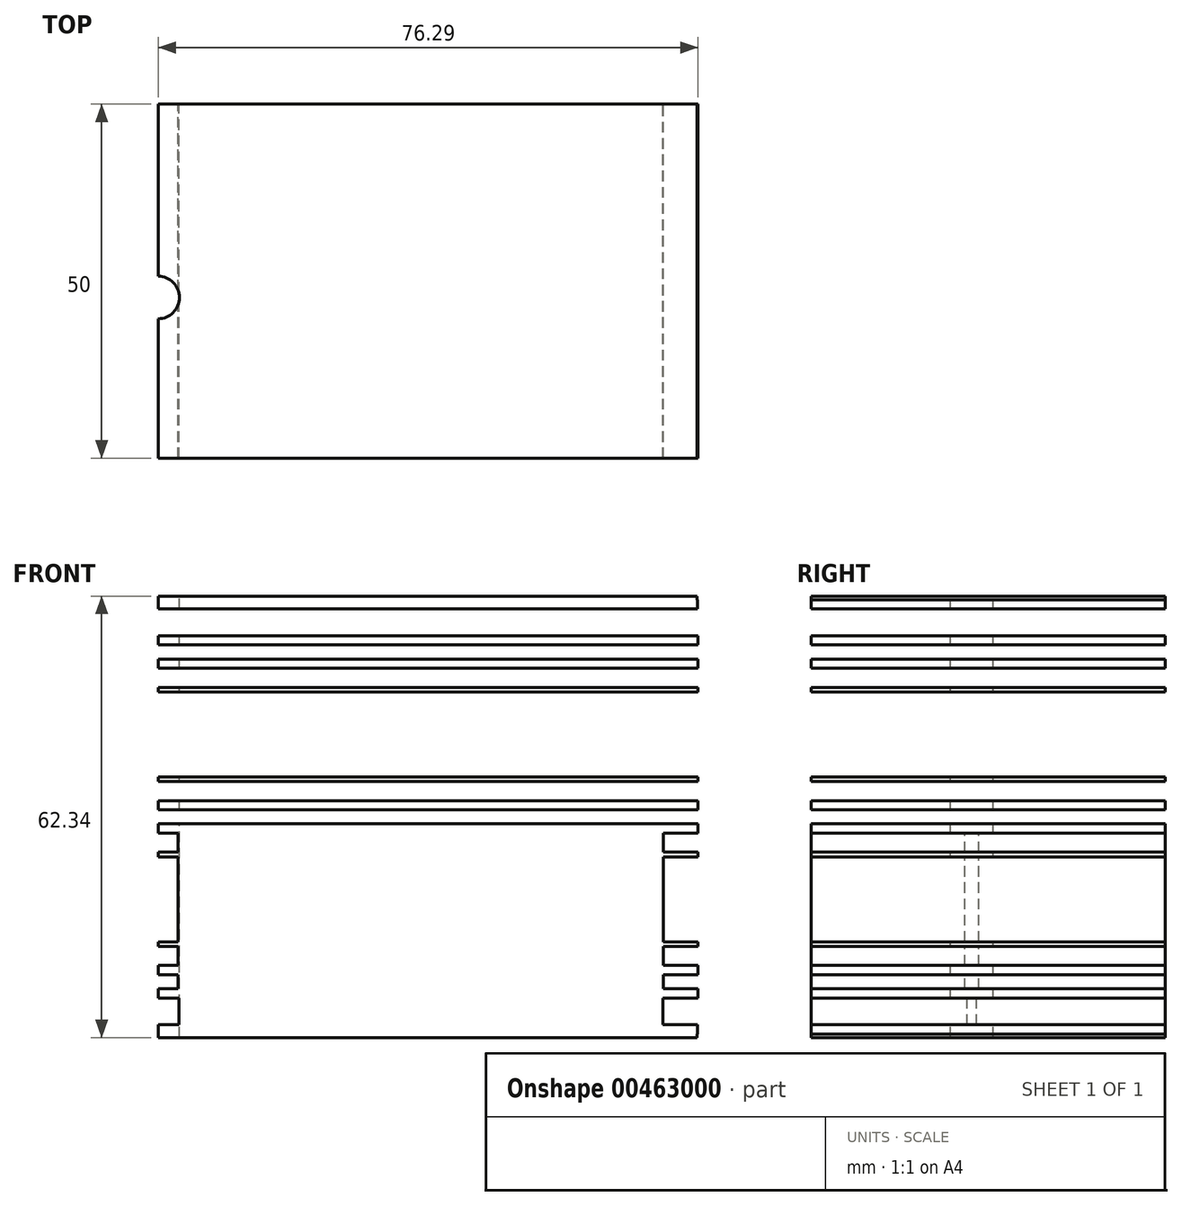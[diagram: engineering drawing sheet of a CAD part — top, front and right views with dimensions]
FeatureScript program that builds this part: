
annotation { "Feature Type Name" : "Feature", "Feature Type Description" : "" }
export const myFeature = defineFeature(function(context is Context, id is Id, definition is map)
    precondition{}
    {
        {
            var Q0;
            Q0=qCreatedBy(makeId("Front.planeOp"),FACE);
            var sketch = newSketch(context, id + "F0", { "sketchPlane" : qUnion([Q0])});
            skLineSegment(sketch, "E0.bottom", {"start": v(0, 0) * mm, "end": v(76.17, 0) * mm});
            skLineSegment(sketch, "E0.top", {"start": v(0, 0.5) * mm, "end": v(76.17, 0.5) * mm});
            skLineSegment(sketch, "E0.left", {"start": v(0, 0) * mm, "end": v(0, 0.5) * mm});
            skLineSegment(sketch, "E0.right", {"start": v(76.17, 0) * mm, "end": v(76.17, 0.5) * mm});
            skLineSegment(sketch, "E1.bottom", {"start": v(0, 0) * mm, "end": v(76.2, 0) * mm});
            skLineSegment(sketch, "E1.top", {"start": v(0, -1.3) * mm, "end": v(76.2, -1.3) * mm});
            skLineSegment(sketch, "E1.left", {"start": v(0, 0) * mm, "end": v(0, -1.3) * mm});
            skLineSegment(sketch, "E1.right", {"start": v(76.2, 0) * mm, "end": v(76.2, -1.3) * mm});
            skLineSegment(sketch, "E2.bottom", {"start": v(2.92, -1.3) * mm, "end": v(71.33, -1.3) * mm});
            skLineSegment(sketch, "E2.top", {"start": v(2.92, -5.07) * mm, "end": v(71.33, -5.07) * mm});
            skLineSegment(sketch, "E2.left", {"start": v(2.92, -1.3) * mm, "end": v(2.92, -5.07) * mm});
            skLineSegment(sketch, "E2.right", {"start": v(71.33, -1.3) * mm, "end": v(71.33, -5.07) * mm});
            skLineSegment(sketch, "E3.bottom", {"start": v(0, -5.07) * mm, "end": v(76.3, -5.07) * mm});
            skLineSegment(sketch, "E3.top", {"start": v(0, -6.37) * mm, "end": v(76.3, -6.37) * mm});
            skLineSegment(sketch, "E3.left", {"start": v(0, -5.07) * mm, "end": v(0, -6.37) * mm});
            skLineSegment(sketch, "E3.right", {"start": v(76.3, -5.07) * mm, "end": v(76.3, -6.37) * mm});
            skLineSegment(sketch, "E4.bottom", {"start": v(2.83, -6.37) * mm, "end": v(71.36, -6.37) * mm});
            skLineSegment(sketch, "E4.top", {"start": v(2.83, -8.37) * mm, "end": v(71.36, -8.37) * mm});
            skLineSegment(sketch, "E4.left", {"start": v(2.83, -6.37) * mm, "end": v(2.83, -8.37) * mm});
            skLineSegment(sketch, "E4.right", {"start": v(71.36, -6.37) * mm, "end": v(71.36, -8.37) * mm});
            skLineSegment(sketch, "E5.bottom", {"start": v(0, -8.37) * mm, "end": v(76.3, -8.37) * mm});
            skLineSegment(sketch, "E5.top", {"start": v(0, -9.67) * mm, "end": v(76.3, -9.67) * mm});
            skLineSegment(sketch, "E5.left", {"start": v(0, -8.37) * mm, "end": v(0, -9.67) * mm});
            skLineSegment(sketch, "E5.right", {"start": v(76.3, -8.37) * mm, "end": v(76.3, -9.67) * mm});
            skLineSegment(sketch, "E6.bottom", {"start": v(2.83, -9.67) * mm, "end": v(71.36, -9.67) * mm});
            skLineSegment(sketch, "E6.top", {"start": v(2.83, -12.37) * mm, "end": v(71.36, -12.37) * mm});
            skLineSegment(sketch, "E6.left", {"start": v(2.83, -9.67) * mm, "end": v(2.83, -12.37) * mm});
            skLineSegment(sketch, "E6.right", {"start": v(71.36, -9.67) * mm, "end": v(71.36, -12.37) * mm});
            skPoint(sketch, "E7.oppositeSnap0", {"position": v(76.3, -9.02) * mm});
            skLineSegment(sketch, "E7.bottom", {"start": v(0, -12.37) * mm, "end": v(76.3, -12.37) * mm});
            skLineSegment(sketch, "E7.top", {"start": v(0, -13.02) * mm, "end": v(76.3, -13.02) * mm});
            skLineSegment(sketch, "E7.left", {"start": v(0, -12.37) * mm, "end": v(0, -13.02) * mm});
            skLineSegment(sketch, "E7.right", {"start": v(76.3, -12.37) * mm, "end": v(76.3, -13.02) * mm});
            skLineSegment(sketch, "E8.bottom", {"start": v(2.83, -13.02) * mm, "end": v(71.36, -13.02) * mm});
            skLineSegment(sketch, "E8.top", {"start": v(2.83, -25.02) * mm, "end": v(71.36, -25.02) * mm});
            skLineSegment(sketch, "E8.left", {"start": v(2.83, -13.02) * mm, "end": v(2.83, -25.02) * mm});
            skLineSegment(sketch, "E8.right", {"start": v(71.36, -13.02) * mm, "end": v(71.36, -25.02) * mm});
            skLineSegment(sketch, "E9.bottom", {"start": v(0, -25.02) * mm, "end": v(76.3, -25.02) * mm});
            skLineSegment(sketch, "E9.top", {"start": v(0, -25.67) * mm, "end": v(76.3, -25.67) * mm});
            skLineSegment(sketch, "E9.left", {"start": v(0, -25.02) * mm, "end": v(0, -25.67) * mm});
            skLineSegment(sketch, "E9.right", {"start": v(76.3, -25.02) * mm, "end": v(76.3, -25.67) * mm});
            skLineSegment(sketch, "E10.bottom", {"start": v(2.83, -25.67) * mm, "end": v(71.36, -25.67) * mm});
            skLineSegment(sketch, "E10.top", {"start": v(2.83, -28.37) * mm, "end": v(71.36, -28.37) * mm});
            skLineSegment(sketch, "E10.left", {"start": v(2.83, -25.67) * mm, "end": v(2.83, -28.37) * mm});
            skLineSegment(sketch, "E10.right", {"start": v(71.36, -25.67) * mm, "end": v(71.36, -28.37) * mm});
            skLineSegment(sketch, "E11.bottom", {"start": v(0, -28.37) * mm, "end": v(76.3, -28.37) * mm});
            skLineSegment(sketch, "E11.top", {"start": v(0, -29.67) * mm, "end": v(76.3, -29.67) * mm});
            skLineSegment(sketch, "E11.left", {"start": v(0, -28.37) * mm, "end": v(0, -29.67) * mm});
            skLineSegment(sketch, "E11.right", {"start": v(76.3, -28.37) * mm, "end": v(76.3, -29.67) * mm});
            skLineSegment(sketch, "E12", {"start": v(-3.37, -30.67) * mm, "end": v(78.4, -30.67) * mm, "construction": true});
            skLineSegment(sketch, "E13.MirrorCS", {"start": v(0, -61.34) * mm, "end": v(0, -61.84) * mm});
            skLineSegment(sketch, "E14.MirrorCS", {"start": v(76.17, -61.34) * mm, "end": v(76.17, -61.84) * mm});
            skLineSegment(sketch, "E15.MirrorCS", {"start": v(0, -36.32) * mm, "end": v(0, -35.67) * mm});
            skLineSegment(sketch, "E16.MirrorCS", {"start": v(76.3, -48.97) * mm, "end": v(76.3, -48.32) * mm});
            skLineSegment(sketch, "E17.MirrorCS", {"start": v(76.3, -32.97) * mm, "end": v(76.3, -31.67) * mm});
            skLineSegment(sketch, "E18.MirrorCS", {"start": v(0, -52.97) * mm, "end": v(0, -51.67) * mm});
            skLineSegment(sketch, "E19.MirrorCS", {"start": v(0, -56.27) * mm, "end": v(0, -54.97) * mm});
            skLineSegment(sketch, "E20.MirrorCS", {"start": v(76.3, -56.27) * mm, "end": v(76.3, -54.97) * mm});
            skLineSegment(sketch, "E21.MirrorCS", {"start": v(0, -61.34) * mm, "end": v(0, -60.04) * mm});
            skLineSegment(sketch, "E22.MirrorCS", {"start": v(76.2, -61.34) * mm, "end": v(76.2, -60.04) * mm});
            skLineSegment(sketch, "E23.MirrorCS", {"start": v(76.3, -52.97) * mm, "end": v(76.3, -51.67) * mm});
            skLineSegment(sketch, "E24.MirrorCS", {"start": v(76.3, -36.32) * mm, "end": v(76.3, -35.67) * mm});
            skLineSegment(sketch, "E25.MirrorCS", {"start": v(0, -48.97) * mm, "end": v(0, -48.32) * mm});
            skLineSegment(sketch, "E26.MirrorCS", {"start": v(0, -32.97) * mm, "end": v(0, -31.67) * mm});
            skLineSegment(sketch, "E27.MirrorCS", {"start": v(0, -61.34) * mm, "end": v(76.17, -61.34) * mm});
            skLineSegment(sketch, "E28.MirrorCS", {"start": v(2.83, -51.67) * mm, "end": v(71.36, -51.67) * mm});
            skLineSegment(sketch, "E29.MirrorCS", {"start": v(2.83, -35.67) * mm, "end": v(71.36, -35.67) * mm});
            skLineSegment(sketch, "E30.MirrorCS", {"start": v(2.92, -56.27) * mm, "end": v(71.33, -56.27) * mm});
            skLineSegment(sketch, "E31.MirrorCS", {"start": v(2.83, -48.32) * mm, "end": v(2.83, -36.32) * mm});
            skLineSegment(sketch, "E32.MirrorCS", {"start": v(2.83, -54.97) * mm, "end": v(2.83, -52.97) * mm});
            skLineSegment(sketch, "E33.MirrorCS", {"start": v(2.83, -35.67) * mm, "end": v(2.83, -32.97) * mm});
            skLineSegment(sketch, "E34.MirrorCS", {"start": v(2.83, -51.67) * mm, "end": v(2.83, -48.97) * mm});
            skLineSegment(sketch, "E35.MirrorCS", {"start": v(71.36, -54.97) * mm, "end": v(71.36, -52.97) * mm});
            skPoint(sketch, "E36.MirrorP", {"position": v(76.3, -52.32) * mm});
            skLineSegment(sketch, "E37.MirrorCS", {"start": v(0, -54.97) * mm, "end": v(76.3, -54.97) * mm});
            skLineSegment(sketch, "E38.MirrorCS", {"start": v(71.36, -48.32) * mm, "end": v(71.36, -36.32) * mm});
            skLineSegment(sketch, "E39.MirrorCS", {"start": v(0, -61.84) * mm, "end": v(76.17, -61.84) * mm});
            skLineSegment(sketch, "E40.MirrorCS", {"start": v(0, -61.34) * mm, "end": v(76.2, -61.34) * mm});
            skLineSegment(sketch, "E41.MirrorCS", {"start": v(0, -60.04) * mm, "end": v(76.2, -60.04) * mm});
            skLineSegment(sketch, "E42.MirrorCS", {"start": v(2.83, -32.97) * mm, "end": v(71.36, -32.97) * mm});
            skLineSegment(sketch, "E43.MirrorCS", {"start": v(2.83, -48.97) * mm, "end": v(71.36, -48.97) * mm});
            skLineSegment(sketch, "E44.MirrorCS", {"start": v(0, -52.97) * mm, "end": v(76.3, -52.97) * mm});
            skLineSegment(sketch, "E45.MirrorCS", {"start": v(71.36, -51.67) * mm, "end": v(71.36, -48.97) * mm});
            skLineSegment(sketch, "E46.MirrorCS", {"start": v(2.83, -36.32) * mm, "end": v(71.36, -36.32) * mm});
            skLineSegment(sketch, "E47.MirrorCS", {"start": v(71.36, -35.67) * mm, "end": v(71.36, -32.97) * mm});
            skLineSegment(sketch, "E48.MirrorCS", {"start": v(0, -56.27) * mm, "end": v(76.3, -56.27) * mm});
            skLineSegment(sketch, "E49.MirrorCS", {"start": v(2.83, -52.97) * mm, "end": v(71.36, -52.97) * mm});
            skLineSegment(sketch, "E50.MirrorCS", {"start": v(71.33, -60.04) * mm, "end": v(71.33, -56.27) * mm});
            skLineSegment(sketch, "E51.MirrorCS", {"start": v(0, -35.67) * mm, "end": v(76.3, -35.67) * mm});
            skLineSegment(sketch, "E52.MirrorCS", {"start": v(0, -51.67) * mm, "end": v(76.3, -51.67) * mm});
            skLineSegment(sketch, "E53.MirrorCS", {"start": v(2.92, -60.04) * mm, "end": v(2.92, -56.27) * mm});
            skLineSegment(sketch, "E54.MirrorCS", {"start": v(0, -32.97) * mm, "end": v(76.3, -32.97) * mm});
            skLineSegment(sketch, "E55.MirrorCS", {"start": v(0, -48.97) * mm, "end": v(76.3, -48.97) * mm});
            skLineSegment(sketch, "E56.MirrorCS", {"start": v(2.83, -48.32) * mm, "end": v(71.36, -48.32) * mm});
            skLineSegment(sketch, "E57.MirrorCS", {"start": v(2.83, -54.97) * mm, "end": v(71.36, -54.97) * mm});
            skLineSegment(sketch, "E58.MirrorCS", {"start": v(0, -36.32) * mm, "end": v(76.3, -36.32) * mm});
            skLineSegment(sketch, "E59.MirrorCS", {"start": v(0, -48.32) * mm, "end": v(76.3, -48.32) * mm});
            skLineSegment(sketch, "E60.MirrorCS", {"start": v(0, -31.67) * mm, "end": v(76.3, -31.67) * mm});
            skLineSegment(sketch, "E61.MirrorCS", {"start": v(2.92, -60.04) * mm, "end": v(71.33, -60.04) * mm});
            skLineSegment(sketch, "E62.bottom", {"start": v(2.83, -29.67) * mm, "end": v(71.36, -29.67) * mm});
            skLineSegment(sketch, "E62.top", {"start": v(2.83, -31.67) * mm, "end": v(71.36, -31.67) * mm});
            skLineSegment(sketch, "E62.left", {"start": v(2.83, -29.67) * mm, "end": v(2.83, -31.67) * mm});
            skLineSegment(sketch, "E62.right", {"start": v(71.36, -29.67) * mm, "end": v(71.36, -31.67) * mm});
            skSolve(sketch);
        }
        {
            var Q0;
            {var subQ3=sQuery(id+"F0.wireOp",EDGE,"E1.left");Q0=makeQuery(id+"F0.imprint","IMPRINT",FACE,{"disambiguationData":[TD([[makeQuery(id+"F0.imprint","IMPRINT",EDGE,{"derivedFrom":subQ3}),1.0]])]});}
            var Q1;
            {var subQ3=sQuery(id+"F0.wireOp",EDGE,"E21.MirrorCS");Q1=makeQuery(id+"F0.imprint","IMPRINT",FACE,{"disambiguationData":[TD([[makeQuery(id+"F0.imprint","IMPRINT",EDGE,{"derivedFrom":subQ3}),-1.0]])]});}
            var Q2;
            {var subQ0=sQuery(id+"F0.wireOp",EDGE,"E3.left");Q2=makeQuery(id+"F0.imprint","IMPRINT",FACE,{"disambiguationData":[TD([[makeQuery(id+"F0.imprint","IMPRINT",EDGE,{"derivedFrom":subQ0}),1.0]])]});}
            var Q3;
            {var subQ0=sQuery(id+"F0.wireOp",EDGE,"E5.left");Q3=makeQuery(id+"F0.imprint","IMPRINT",FACE,{"disambiguationData":[TD([[makeQuery(id+"F0.imprint","IMPRINT",EDGE,{"derivedFrom":subQ0}),1.0]])]});}
            var Q4;
            {var subQ4=sQuery(id+"F0.wireOp",EDGE,"E18.MirrorCS");Q4=makeQuery(id+"F0.imprint","IMPRINT",FACE,{"disambiguationData":[TD([[makeQuery(id+"F0.imprint","IMPRINT",EDGE,{"derivedFrom":subQ4}),-1.0]])]});}
            var Q5;
            {var subQ0=sQuery(id+"F0.wireOp",EDGE,"E7.left");Q5=makeQuery(id+"F0.imprint","IMPRINT",FACE,{"disambiguationData":[TD([[makeQuery(id+"F0.imprint","IMPRINT",EDGE,{"derivedFrom":subQ0}),1.0]])]});}
            var Q6;
            {var subQ0=sQuery(id+"F0.wireOp",EDGE,"E9.left");Q6=makeQuery(id+"F0.imprint","IMPRINT",FACE,{"disambiguationData":[TD([[makeQuery(id+"F0.imprint","IMPRINT",EDGE,{"derivedFrom":subQ0}),1.0]])]});}
            var Q7;
            {var subQ4=sQuery(id+"F0.wireOp",EDGE,"E19.MirrorCS");Q7=makeQuery(id+"F0.imprint","IMPRINT",FACE,{"disambiguationData":[TD([[makeQuery(id+"F0.imprint","IMPRINT",EDGE,{"derivedFrom":subQ4}),-1.0]])]});}
            var Q8;
            {var subQ4=sQuery(id+"F0.wireOp",EDGE,"E17.MirrorCS");Q8=makeQuery(id+"F0.imprint","IMPRINT",FACE,{"disambiguationData":[TD([[makeQuery(id+"F0.imprint","IMPRINT",EDGE,{"derivedFrom":subQ4}),1.0]])]});}
            var Q9;
            {var subQ0=sQuery(id+"F0.wireOp",EDGE,"E11.left");Q9=makeQuery(id+"F0.imprint","IMPRINT",FACE,{"disambiguationData":[TD([[makeQuery(id+"F0.imprint","IMPRINT",EDGE,{"derivedFrom":subQ0}),1.0]])]});}
            var Q10;
            Q10=makeQuery(id+"F0.imprint","IMPRINT",FACE,{"disambiguationData":[TD([[makeQuery(id+"F0.imprint","IMPRINT",EDGE,{"derivedFrom":sQuery(id+"F0.wireOp",EDGE,"E0.top")}),-1.0]])]});
            var Q11;
            {var subQ0=sQuery(id+"F0.wireOp",EDGE,"E13.MirrorCS");Q11=makeQuery(id+"F0.imprint","IMPRINT",FACE,{"disambiguationData":[TD([[makeQuery(id+"F0.imprint","IMPRINT",EDGE,{"derivedFrom":subQ0}),1.0]])]});}
            var Q12;
            {var subQ4=sQuery(id+"F0.wireOp",EDGE,"E16.MirrorCS");Q12=makeQuery(id+"F0.imprint","IMPRINT",FACE,{"disambiguationData":[TD([[makeQuery(id+"F0.imprint","IMPRINT",EDGE,{"derivedFrom":subQ4}),1.0]])]});}
            var Q13;
            {var subQ1=sQuery(id+"F0.wireOp",EDGE,"E15.MirrorCS");Q13=makeQuery(id+"F0.imprint","IMPRINT",FACE,{"disambiguationData":[TD([[makeQuery(id+"F0.imprint","IMPRINT",EDGE,{"derivedFrom":subQ1}),-1.0]])]});}
            var Q14;
            {var subQ0=sQuery(id+"F0.wireOp",EDGE,"E50.MirrorCS");Q14=makeQuery(id+"F0.imprint","IMPRINT",FACE,{"disambiguationData":[TD([[makeQuery(id+"F0.imprint","IMPRINT",EDGE,{"derivedFrom":subQ0}),1.0]])]});}
            var Q15;
            Q15=makeQuery(id+"F0.imprint","IMPRINT",FACE,{"disambiguationData":[TD([[makeQuery(id+"F0.imprint","IMPRINT",EDGE,{"derivedFrom":sQuery(id+"F0.wireOp",EDGE,"E6.bottom")}),-1.0]])]});
            var Q16;
            Q16=makeQuery(id+"F0.imprint","IMPRINT",FACE,{"disambiguationData":[TD([[makeQuery(id+"F0.imprint","IMPRINT",EDGE,{"derivedFrom":sQuery(id+"F0.wireOp",EDGE,"E4.bottom")}),-1.0]])]});
            var Q17;
            {var subQ0=sQuery(id+"F0.wireOp",EDGE,"E31.MirrorCS");Q17=makeQuery(id+"F0.imprint","IMPRINT",FACE,{"disambiguationData":[TD([[makeQuery(id+"F0.imprint","IMPRINT",EDGE,{"derivedFrom":subQ0}),-1.0]])]});}
            var Q18;
            {var subQ0=sQuery(id+"F0.wireOp",EDGE,"E33.MirrorCS");Q18=makeQuery(id+"F0.imprint","IMPRINT",FACE,{"disambiguationData":[TD([[makeQuery(id+"F0.imprint","IMPRINT",EDGE,{"derivedFrom":subQ0}),-1.0]])]});}
            var Q19;
            Q19=makeQuery(id+"F0.imprint","IMPRINT",FACE,{"disambiguationData":[TD([[makeQuery(id+"F0.imprint","IMPRINT",EDGE,{"derivedFrom":sQuery(id+"F0.wireOp",EDGE,"E32.MirrorCS")}),-1.0]])]});
            var Q20;
            Q20=makeQuery(id+"F0.imprint","IMPRINT",FACE,{"disambiguationData":[TD([[makeQuery(id+"F0.imprint","IMPRINT",EDGE,{"derivedFrom":sQuery(id+"F0.wireOp",EDGE,"E10.bottom")}),-1.0]])]});
            var Q21;
            Q21=makeQuery(id+"F0.imprint","IMPRINT",FACE,{"disambiguationData":[TD([[makeQuery(id+"F0.imprint","IMPRINT",EDGE,{"derivedFrom":sQuery(id+"F0.wireOp",EDGE,"E62.bottom")}),-1.0]])]});
            var Q22;
            Q22=makeQuery(id+"F0.imprint","IMPRINT",FACE,{"disambiguationData":[TD([[makeQuery(id+"F0.imprint","IMPRINT",EDGE,{"derivedFrom":sQuery(id+"F0.wireOp",EDGE,"E8.bottom")}),-1.0]])]});
            var Q23;
            {var subQ0=sQuery(id+"F0.wireOp",EDGE,"E34.MirrorCS");Q23=makeQuery(id+"F0.imprint","IMPRINT",FACE,{"disambiguationData":[TD([[makeQuery(id+"F0.imprint","IMPRINT",EDGE,{"derivedFrom":subQ0}),-1.0]])]});}
            var Q24;
            Q24=makeQuery(id+"F0.imprint","IMPRINT",FACE,{"disambiguationData":[TD([[makeQuery(id+"F0.imprint","IMPRINT",EDGE,{"derivedFrom":sQuery(id+"F0.wireOp",EDGE,"E2.bottom")}),-1.0]])]});
            extrude(context, id + "F1", {"entities" : qUnion([Q0, Q1, Q2, Q3, Q4, Q5, Q6, Q7, Q8, Q9, Q10, Q11, Q12, Q13, Q14, Q15, Q16, Q17, Q18, Q19, Q20, Q21, Q22, Q23, Q24]), "depth" : 50 * mm});
        }
        {
            var Q0;
            Q0=qCreatedBy(makeId("Top.planeOp"),FACE);
            var sketch = newSketch(context, id + "F2", { "sketchPlane" : qUnion([Q0])});
            skCircle(sketch, "E63", {"center": v(0, -27.3) * mm, "radius": 3 * mm});
            skSolve(sketch);
        }
        {
            var Q0;
            Q0 = qSketchRegion(id + "F2", true);
            extrude(context, id + "F3", {"entities" : qUnion([Q0]), "operationType" : NewBodyOperationType.REMOVE, "oppositeDirection" : true, "depth" : 70 * mm, "hasSecondDirection" : true, "secondDirectionBound" : SecondDirectionBoundingType.THROUGH_ALL, "secondDirectionOppositeDirection" : false, "secondDirectionDepth" : 25 * mm});
        }
    });
